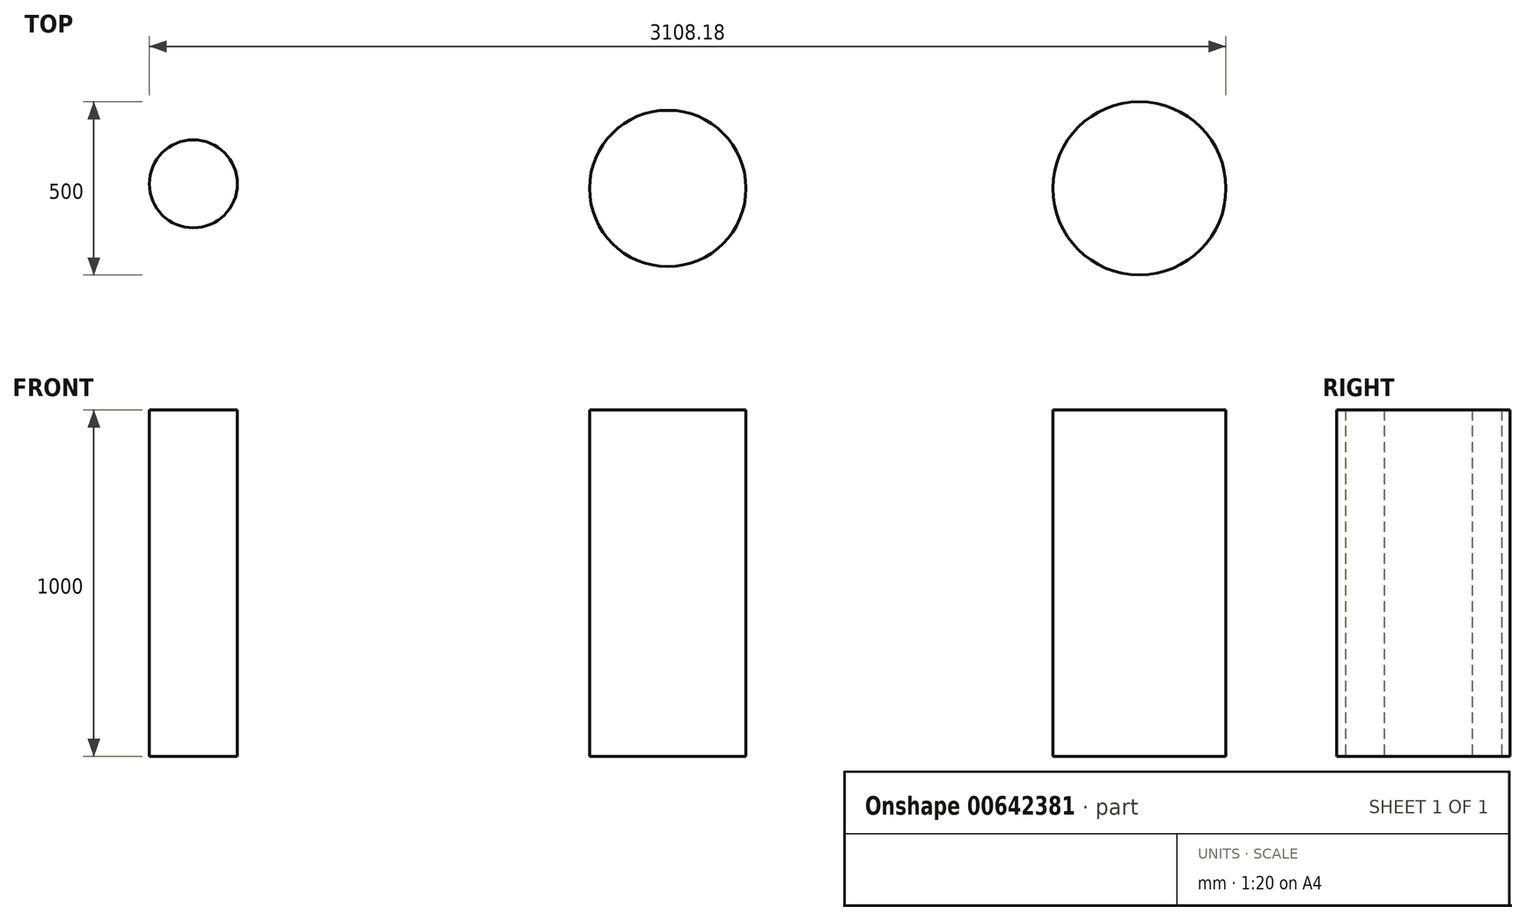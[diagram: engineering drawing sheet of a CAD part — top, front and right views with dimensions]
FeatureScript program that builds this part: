
annotation { "Feature Type Name" : "Feature", "Feature Type Description" : "" }
export const myFeature = defineFeature(function(context is Context, id is Id, definition is map)
    precondition{}
    {
        {
            var Q0;
            Q0=qCreatedBy(makeId("Top.planeOp"),FACE);
            var sketch = newSketch(context, id + "F0", { "sketchPlane" : qUnion([Q0])});
            skCircle(sketch, "E0", {"center": v(-132.67, 13.25) * mm, "radius": 127 * mm});
            skCircle(sketch, "E1", {"center": v(407.01, 0) * mm, "radius": 225.77 * mm});
            skCircle(sketch, "E2", {"center": v(1208.5, 0) * mm, "radius": 250 * mm});
            skSolve(sketch);
        }
        {
            var Q0;
            Q0=makeQuery(id+"F0.imprint","IMPRINT",FACE,{"disambiguationData":[TD([[makeQuery(id+"F0.imprint","IMPRINT",EDGE,{"derivedFrom":sQuery(id+"F0.wireOp",EDGE,"E0")}),1.0]])]});
            var Q1;
            Q1=makeQuery(id+"F0.imprint","IMPRINT",FACE,{"disambiguationData":[TD([[makeQuery(id+"F0.imprint","IMPRINT",EDGE,{"derivedFrom":sQuery(id+"F0.wireOp",EDGE,"E1")}),1.0]])]});
            var Q2;
            Q2=makeQuery(id+"F0.imprint","IMPRINT",FACE,{"disambiguationData":[TD([[makeQuery(id+"F0.imprint","IMPRINT",EDGE,{"derivedFrom":sQuery(id+"F0.wireOp",EDGE,"E2")}),1.0]])]});
            extrude(context, id + "F1", {"entities" : qUnion([Q0, Q1, Q2]), "depth" : 1000 * mm, "offsetDistance" : 25 * mm});
        }
        {
            var Q0;
            Q0=makeQuery(id+"F1.opExtrude","SWEPT_BODY",BODY,{"disambiguationData":[OSD([sQuery(id+"F0.wireOp",EDGE,"E2")])]});
            transform(context, id + "F2", {"entities" : qUnion([Q0]), "transformType" : TransformType.TRANSLATION_3D, "dx" : 1390 * mm, "dy" : 0 * mm, "dz" : 0 * mm, "makeCopy" : false});
        }
        {
            var Q0;
            Q0=makeQuery(id+"F1.opExtrude","SWEPT_BODY",BODY,{"disambiguationData":[OSD([sQuery(id+"F0.wireOp",EDGE,"E1")])]});
            transform(context, id + "F3", {"entities" : qUnion([Q0]), "transformType" : TransformType.TRANSLATION_3D, "dx" : 830 * mm, "dy" : 0 * mm, "dz" : 0 * mm, "makeCopy" : false});
        }
    });
